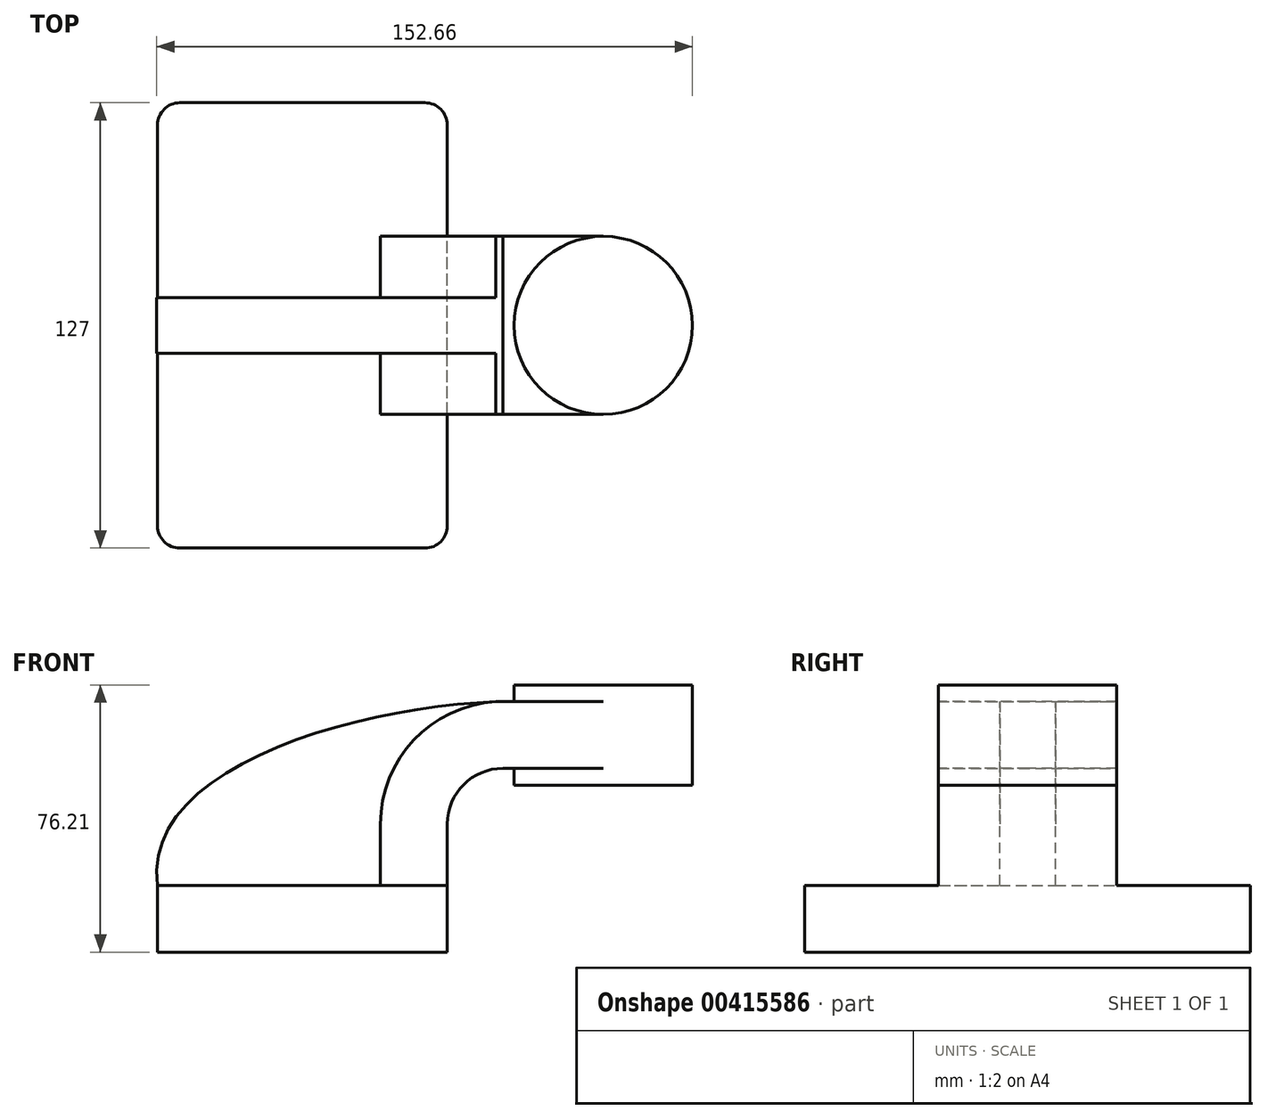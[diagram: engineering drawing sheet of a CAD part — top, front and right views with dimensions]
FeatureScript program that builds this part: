
annotation { "Feature Type Name" : "Feature", "Feature Type Description" : "" }
export const myFeature = defineFeature(function(context is Context, id is Id, definition is map)
    precondition{}
    {
        {
            var Q0;
            Q0=qCreatedBy(makeId("Front.planeOp"),FACE);
            var sketch = newSketch(context, id + "F0", { "sketchPlane" : qUnion([Q0])});
            skLineSegment(sketch, "E0.bottom", {"start": v(41.27, 9.53) * mm, "end": v(-41.28, 9.53) * mm});
            skLineSegment(sketch, "E0.top", {"start": v(41.28, -9.52) * mm, "end": v(-41.27, -9.52) * mm});
            skLineSegment(sketch, "E0.left", {"start": v(41.27, 9.53) * mm, "end": v(41.28, -9.52) * mm});
            skLineSegment(sketch, "E0.right", {"start": v(-41.28, 9.53) * mm, "end": v(-41.27, -9.52) * mm});
            skPoint(sketch, "E0.middle", {"position": v(0, 0) * mm});
            skLineSegment(sketch, "E1.bottom", {"start": v(111.12, 38.1) * mm, "end": v(60.32, 38.1) * mm});
            skLineSegment(sketch, "E1.top", {"start": v(111.12, 66.68) * mm, "end": v(60.33, 66.68) * mm});
            skLineSegment(sketch, "E1.left", {"start": v(111.12, 38.1) * mm, "end": v(111.12, 66.68) * mm});
            skLineSegment(sketch, "E1.right", {"start": v(60.32, 38.1) * mm, "end": v(60.32, 66.68) * mm});
            skPoint(sketch, "E1.middle", {"position": v(85.72, 52.39) * mm});
            skLineSegment(sketch, "E2", {"start": v(41.27, 9.53) * mm, "end": v(41.27, 27) * mm});
            skArc(sketch, "E3", {"start": v(41.27, 27) * mm, "mid": v(45.92, 38.23) * mm, "end": v(57.15, 42.88) * mm});
            skLineSegment(sketch, "E4", {"start": v(57.15, 42.88) * mm, "end": v(85.72, 42.88) * mm});
            skLineSegment(sketch, "E5.0", {"start": v(57.15, 61.93) * mm, "end": v(85.72, 61.93) * mm});
            skArc(sketch, "E5.1", {"start": v(22.22, 27) * mm, "mid": v(32.45, 51.7) * mm, "end": v(57.15, 61.93) * mm});
            skLineSegment(sketch, "E5.2", {"start": v(22.22, 9.53) * mm, "end": v(22.22, 27) * mm});
            skFitSpline(sketch, "E6", {"points": [v(-41.28, 9.53) * mm, v(57.15, 61.93) * mm], "startDerivative": vector(-14.43, 102.72) * mm, "endDerivative": vector(119.38, 2.8) * mm});
            skLineSegment(sketch, "E7", {"start": v(85.72, 38.1) * mm, "end": v(85.72, 66.68) * mm});
            skSolve(sketch);
        }
        {
            var Q0;
            Q0=makeQuery(id+"F0.imprint","IMPRINT",FACE,{"disambiguationData":[TD([[makeQuery(id+"F0.imprint","IMPRINT",EDGE,{"derivedFrom":sQuery(id+"F0.wireOp",EDGE,"E0.top")}),-1.0]])]});
            extrude(context, id + "F1", {"entities" : qUnion([Q0]), "endBound" : BoundingType.SYMMETRIC, "depth" : 127 * mm});
        }
        {
            var Q0;
            {var subQ6=sQuery(id+"F0.wireOp",EDGE,"E2");Q0=makeQuery(id+"F0.imprint","IMPRINT",FACE,{"disambiguationData":[TD([[makeQuery(id+"F0.imprint","IMPRINT",EDGE,{"derivedFrom":subQ6}),1.0]])]});}
            var Q1;
            {var subQ0=sQuery(id+"F0.wireOp",EDGE,"E4");var subQ1=sQuery(id+"F0.wireOp",EDGE,"E1.right");var subQ2=makeQuery(id+"F0.imprint","INTERSECT",VERTEX,{"derivedFrom":[subQ1,subQ0]});Q1=makeQuery(id+"F0.imprint","IMPRINT",FACE,{"disambiguationData":[TD([[makeQuery(id+"F0.imprint","IMPRINT",EDGE,{"disambiguationData":[TD([[subQ2,-1.0]])],"derivedFrom":subQ1}),-1.0]])]});}
            extrude(context, id + "F2", {"entities" : qUnion([Q0, Q1]), "operationType" : NewBodyOperationType.ADD, "endBound" : BoundingType.SYMMETRIC, "depth" : 50.8 * mm});
        }
        {
            var Q0;
            {var subQ3=sQuery(id+"F0.wireOp",EDGE,"E5.2");Q0=makeQuery(id+"F0.imprint","IMPRINT",FACE,{"disambiguationData":[TD([[makeQuery(id+"F0.imprint","IMPRINT",EDGE,{"derivedFrom":subQ3}),1.0]])]});}
            extrude(context, id + "F3", {"entities" : qUnion([Q0]), "operationType" : NewBodyOperationType.ADD, "endBound" : BoundingType.SYMMETRIC, "depth" : 15.88 * mm});
        }
        {
            var Q0;
            {var subQ4=sQuery(id+"F0.wireOp",EDGE,"E1.left");Q0=makeQuery(id+"F0.imprint","IMPRINT",FACE,{"disambiguationData":[TD([[makeQuery(id+"F0.imprint","IMPRINT",EDGE,{"derivedFrom":subQ4}),1.0]])]});}
            var Q1;
            Q1=sQuery(id+"F0.wireOp",EDGE,"E7");
            revolve(context, id + "F4", {"operationType" : NewBodyOperationType.ADD, "entities" : qUnion([Q0]), "axis" : qUnion([Q1]), "revolveType" : RevolveType.FULL});
        }
        {
            var Q0;
            Q0=makeQuery(id+"F1.opExtrude","CAP_EDGE",EDGE,{"disambiguationData":[OSD([sQuery(id+"F0.wireOp",EDGE,"E0.left")])],"isStart":false});
            var Q1;
            Q1=makeQuery(id+"F1.opExtrude","CAP_EDGE",EDGE,{"disambiguationData":[OSD([sQuery(id+"F0.wireOp",EDGE,"E0.right")])],"isStart":false});
            var Q2;
            Q2=makeQuery(id+"F1.opExtrude","CAP_EDGE",EDGE,{"disambiguationData":[OSD([sQuery(id+"F0.wireOp",EDGE,"E0.right")])],"isStart":true});
            var Q3;
            Q3=makeQuery(id+"F1.opExtrude","CAP_EDGE",EDGE,{"disambiguationData":[OSD([sQuery(id+"F0.wireOp",EDGE,"E0.left")])],"isStart":true});
            fillet(context, id + "F5", {"entities" : qUnion([Q0, Q1, Q2, Q3]), "radius" : 6.35 * mm, "tangentPropagation" : true, "allowEdgeOverflow" : false});
        }
    });
